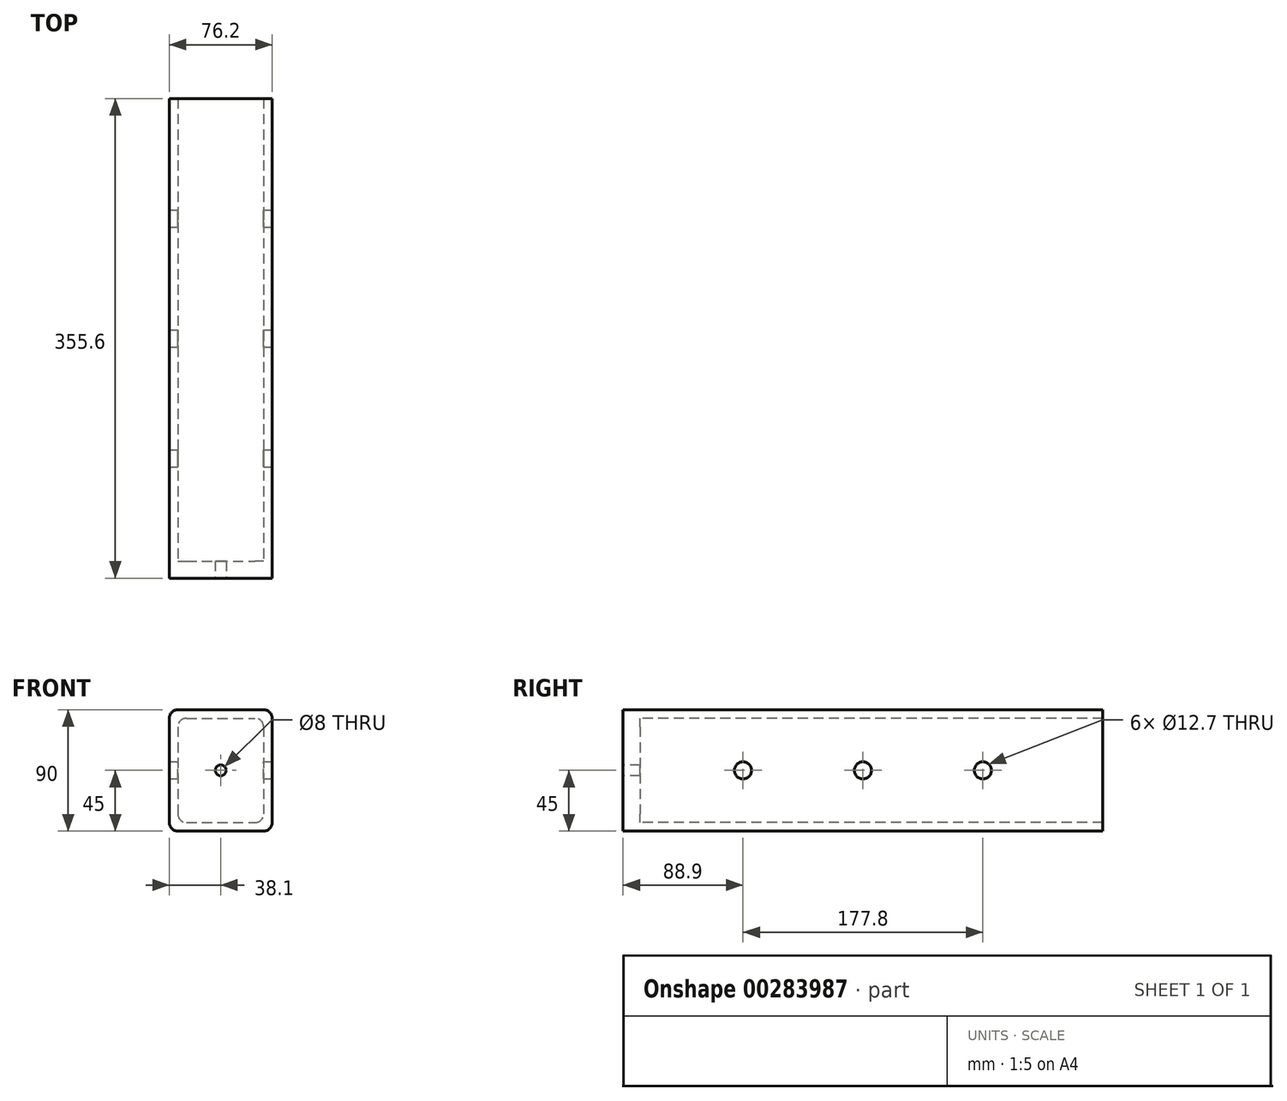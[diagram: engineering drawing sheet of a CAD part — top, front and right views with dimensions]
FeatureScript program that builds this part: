
annotation { "Feature Type Name" : "Feature", "Feature Type Description" : "" }
export const myFeature = defineFeature(function(context is Context, id is Id, definition is map)
    precondition{}
    {
        {
            var Q0;
            Q0=qCreatedBy(makeId("Front.planeOp"),FACE);
            var sketch = newSketch(context, id + "F0", { "sketchPlane" : qUnion([Q0])});
            skLineSegment(sketch, "E0.bottom", {"start": v(31.75, -45) * mm, "end": v(-31.75, -45) * mm});
            skLineSegment(sketch, "E0.top", {"start": v(31.75, 45) * mm, "end": v(-31.75, 45) * mm});
            skLineSegment(sketch, "E0.left", {"start": v(38.1, -38.65) * mm, "end": v(38.1, 38.65) * mm});
            skLineSegment(sketch, "E0.right", {"start": v(-38.1, -38.65) * mm, "end": v(-38.1, 38.65) * mm});
            skPoint(sketch, "E0.middle", {"position": v(0, 0) * mm});
            skLineSegment(sketch, "E1.bottom", {"start": v(25.4, -38.65) * mm, "end": v(-25.4, -38.65) * mm});
            skLineSegment(sketch, "E1.top", {"start": v(25.4, 38.65) * mm, "end": v(-25.4, 38.65) * mm});
            skLineSegment(sketch, "E1.left", {"start": v(31.75, -32.3) * mm, "end": v(31.75, 32.3) * mm});
            skLineSegment(sketch, "E1.right", {"start": v(-31.75, -32.3) * mm, "end": v(-31.75, 32.3) * mm});
            skPoint(sketch, "E2.visualSharp", {"position": v(-38.1, 45) * mm});
            skArc(sketch, "E2.filletArc", {"start": v(-31.75, 45) * mm, "mid": v(-36.24, 43.14) * mm, "end": v(-38.1, 38.65) * mm});
            skArc(sketch, "E3.filletArc", {"start": v(-25.4, 38.65) * mm, "mid": v(-29.9, 36.8) * mm, "end": v(-31.75, 32.3) * mm});
            skPoint(sketch, "E4.visualSharp", {"position": v(31.75, 38.65) * mm});
            skArc(sketch, "E4.filletArc", {"start": v(31.75, 32.3) * mm, "mid": v(29.9, 36.8) * mm, "end": v(25.4, 38.65) * mm});
            skPoint(sketch, "E5.visualSharp", {"position": v(38.1, 45) * mm});
            skArc(sketch, "E5.filletArc", {"start": v(38.1, 38.65) * mm, "mid": v(36.24, 43.14) * mm, "end": v(31.75, 45) * mm});
            skPoint(sketch, "E6.visualSharp", {"position": v(31.75, -38.65) * mm});
            skArc(sketch, "E6.filletArc", {"start": v(25.4, -38.65) * mm, "mid": v(29.9, -36.8) * mm, "end": v(31.75, -32.3) * mm});
            skPoint(sketch, "E7.visualSharp", {"position": v(38.1, -45) * mm});
            skArc(sketch, "E7.filletArc", {"start": v(31.75, -45) * mm, "mid": v(36.24, -43.14) * mm, "end": v(38.1, -38.65) * mm});
            skPoint(sketch, "E8.visualSharp", {"position": v(-31.75, -38.65) * mm});
            skArc(sketch, "E8.filletArc", {"start": v(-31.75, -32.3) * mm, "mid": v(-29.9, -36.8) * mm, "end": v(-25.4, -38.65) * mm});
            skPoint(sketch, "E9.visualSharp", {"position": v(-38.1, -45) * mm});
            skArc(sketch, "E9.filletArc", {"start": v(-38.1, -38.65) * mm, "mid": v(-36.24, -43.14) * mm, "end": v(-31.75, -45) * mm});
            skCircle(sketch, "E10", {"center": v(0, 0) * mm, "radius": 4 * mm});
            skSolve(sketch);
        }
        {
            var Q0;
            Q0=makeQuery(id+"F0.imprint","IMPRINT",FACE,{"disambiguationData":[TD([[makeQuery(id+"F0.imprint","IMPRINT",EDGE,{"derivedFrom":sQuery(id+"F0.wireOp",EDGE,"E1.bottom")}),-1.0]])]});
            extrude(context, id + "F1", {"entities" : qUnion([Q0]), "oppositeDirection" : true, "depth" : 6.35 * mm});
        }
        {
            var Q0;
            Q0=makeQuery(id+"F0.imprint","IMPRINT",FACE,{"disambiguationData":[TD([[makeQuery(id+"F0.imprint","IMPRINT",EDGE,{"derivedFrom":sQuery(id+"F0.wireOp",EDGE,"E0.bottom")}),-1.0]])]});
            extrude(context, id + "F2", {"entities" : qUnion([Q0]), "operationType" : NewBodyOperationType.ADD, "oppositeDirection" : true, "depth" : 355.6 * mm});
        }
        {
            var Q0;
            Q0=qCreatedBy(makeId("Front.planeOp"),FACE);
            var sketch = newSketch(context, id + "F3", { "sketchPlane" : qUnion([Q0])});
            skLineSegment(sketch, "E11.bottom", {"start": v(38.1, -101.6) * mm, "end": v(-38.1, -101.6) * mm});
            skLineSegment(sketch, "E11.top", {"start": v(38.1, 101.6) * mm, "end": v(-38.1, 101.6) * mm});
            skLineSegment(sketch, "E11.left", {"start": v(38.1, -101.6) * mm, "end": v(38.1, 101.6) * mm});
            skLineSegment(sketch, "E11.right", {"start": v(-38.1, -101.6) * mm, "end": v(-38.1, 101.6) * mm});
            skPoint(sketch, "E11.middle", {"position": v(0, 0) * mm});
            skLineSegment(sketch, "E12.bottom", {"start": v(31.75, -95.25) * mm, "end": v(-31.75, -95.25) * mm});
            skLineSegment(sketch, "E12.top", {"start": v(31.75, 95.25) * mm, "end": v(-31.75, 95.25) * mm});
            skLineSegment(sketch, "E12.left", {"start": v(31.75, -95.25) * mm, "end": v(31.75, 95.25) * mm});
            skLineSegment(sketch, "E12.right", {"start": v(-31.75, -95.25) * mm, "end": v(-31.75, 95.25) * mm});
            skSolve(sketch);
        }
        {
            var Q0;
            Q0=makeQuery(id+"F0.imprint","IMPRINT",FACE,{"disambiguationData":[TD([[makeQuery(id+"F0.imprint","IMPRINT",EDGE,{"derivedFrom":sQuery(id+"F0.wireOp",EDGE,"E1.right")}),-1.0]])]});
            var Q1;
            Q1=makeQuery(id+"F0.imprint","IMPRINT",FACE,{"disambiguationData":[TD([[makeQuery(id+"F0.imprint","IMPRINT",EDGE,{"derivedFrom":sQuery(id+"F0.wireOp",EDGE,"E1.left")}),1.0]])]});
            var Q2;
            {var subQ0=sQuery(id+"F0.wireOp",EDGE,"TLKqnz1r-1FyS-fU34-mWic-j3vFf0crAy8C");Q2=makeQuery(id+"F0.imprint","IMPRINT",FACE,{"disambiguationData":[TD([[makeQuery(id+"F0.imprint","IMPRINT",EDGE,{"derivedFrom":subQ0}),-1.0]])]});}
            var Q3;
            Q3=makeQuery(id+"F0.imprint","IMPRINT",FACE,{"disambiguationData":[TD([[makeQuery(id+"F0.imprint","IMPRINT",EDGE,{"derivedFrom":sQuery(id+"F0.wireOp",EDGE,"E0.bottom")}),-1.0]])]});
            extrude(context, id + "F4", {"entities" : qUnion([Q0, Q1, Q2, Q3]), "operationType" : NewBodyOperationType.ADD, "oppositeDirection" : true, "depth" : 12.7 * mm});
        }
        {
            var Q0;
            Q0=makeQuery(id+"F2.opExtrude","SWEPT_FACE",FACE,{"disambiguationData":[OSD([sQuery(id+"F0.wireOp",EDGE,"E0.left")])]});
            var sketch = newSketch(context, id + "F5", { "sketchPlane" : qUnion([Q0])});
            skCircle(sketch, "E13", {"center": v(88.9, 0) * mm, "radius": 6.35 * mm});
            skCircle(sketch, "E14", {"center": v(177.8, 0) * mm, "radius": 6.35 * mm});
            skCircle(sketch, "E15", {"center": v(266.7, 0) * mm, "radius": 6.35 * mm});
            skSolve(sketch);
        }
        {
            var Q0;
            Q0=makeQuery(id+"F5.imprint","IMPRINT",FACE,{"disambiguationData":[TD([[makeQuery(id+"F5.imprint","IMPRINT",EDGE,{"derivedFrom":sQuery(id+"F5.wireOp",EDGE,"E13")}),1.0]])]});
            var Q1;
            Q1=makeQuery(id+"F5.imprint","IMPRINT",FACE,{"disambiguationData":[TD([[makeQuery(id+"F5.imprint","IMPRINT",EDGE,{"derivedFrom":sQuery(id+"F5.wireOp",EDGE,"E14")}),1.0]])]});
            var Q2;
            Q2=makeQuery(id+"F5.imprint","IMPRINT",FACE,{"disambiguationData":[TD([[makeQuery(id+"F5.imprint","IMPRINT",EDGE,{"derivedFrom":sQuery(id+"F5.wireOp",EDGE,"E15")}),1.0]])]});
            extrude(context, id + "F6", {"entities" : qUnion([Q0, Q1, Q2]), "operationType" : NewBodyOperationType.REMOVE, "endBound" : BoundingType.THROUGH_ALL, "oppositeDirection" : true, "depth" : 25.4 * mm});
        }
    });
